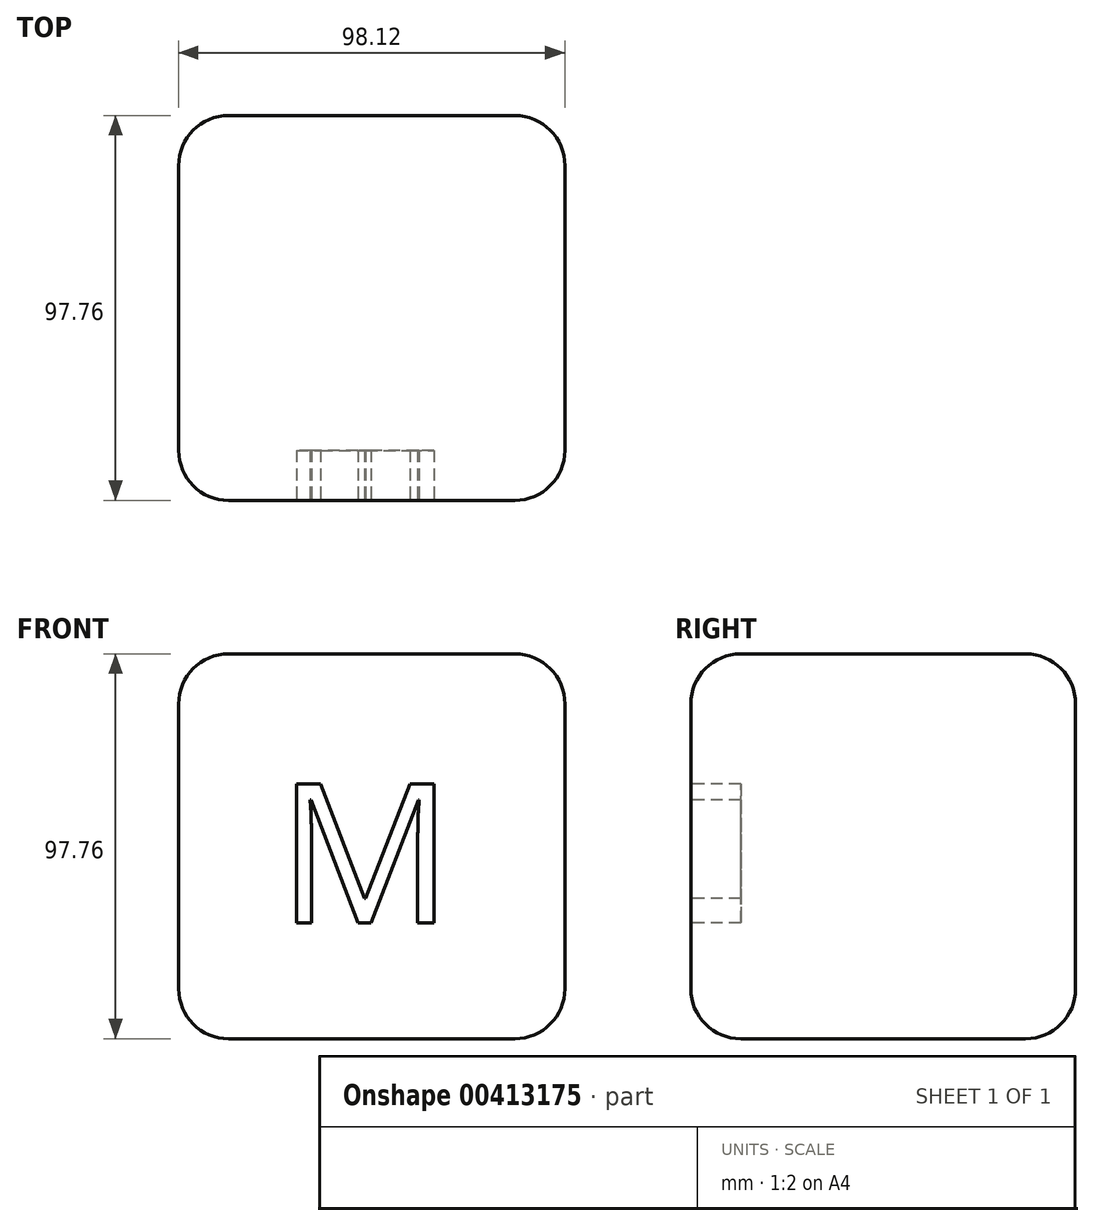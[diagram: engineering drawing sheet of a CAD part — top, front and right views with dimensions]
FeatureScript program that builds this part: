
annotation { "Feature Type Name" : "Feature", "Feature Type Description" : "" }
export const myFeature = defineFeature(function(context is Context, id is Id, definition is map)
    precondition{}
    {
        {
            var Q0;
            Q0=qCreatedBy(makeId("Top.planeOp"),FACE);
            var sketch = newSketch(context, id + "F0", { "sketchPlane" : qUnion([Q0])});
            skLineSegment(sketch, "E0.bottom", {"start": v(-49.06, 48.88) * mm, "end": v(49.06, 48.88) * mm});
            skLineSegment(sketch, "E0.top", {"start": v(-49.06, -48.88) * mm, "end": v(49.06, -48.88) * mm});
            skLineSegment(sketch, "E0.left", {"start": v(-49.06, 48.88) * mm, "end": v(-49.06, -48.88) * mm});
            skLineSegment(sketch, "E0.right", {"start": v(49.06, 48.88) * mm, "end": v(49.06, -48.88) * mm});
            skPoint(sketch, "E0.middle", {"position": v(0, 0) * mm});
            skSolve(sketch);
        }
        {
            var Q0;
            Q0=makeQuery(id+"F0.imprint","IMPRINT",FACE,{"disambiguationData":[TD([[makeQuery(id+"F0.imprint","IMPRINT",EDGE,{"derivedFrom":sQuery(id+"F0.wireOp",EDGE,"E0.bottom")}),-1.0]])]});
            extrude(context, id + "F1", {"entities" : qUnion([Q0]), "depth" : 97.76 * mm});
        }
        {
            var Q0;
            Q0=makeQuery(id+"F1.opExtrude","CAP_EDGE",EDGE,{"disambiguationData":[OSD([sQuery(id+"F0.wireOp",EDGE,"E0.bottom")])],"isStart":false});
            fillet(context, id + "F2", {"entities" : qUnion([Q0]), "radius" : 12.7 * mm, "tangentPropagation" : true, "allowEdgeOverflow" : false});
        }
        {
            var Q0;
            Q0=makeQuery(id+"F1.opExtrude","CAP_EDGE",EDGE,{"disambiguationData":[OSD([sQuery(id+"F0.wireOp",EDGE,"E0.right")])],"isStart":false});
            var Q1;
            Q1=makeQuery(id+"F1.opExtrude","SWEPT_EDGE",EDGE,{"disambiguationData":[OSD([sQuery(id+"F0.wireOp",EDGE,"E0.top"),sQuery(id+"F0.wireOp",EDGE,"E0.right")])]});
            var Q2;
            Q2=makeQuery(id+"F1.opExtrude","CAP_EDGE",EDGE,{"disambiguationData":[OSD([sQuery(id+"F0.wireOp",EDGE,"E0.right")])],"isStart":true});
            var Q3;
            Q3=makeQuery(id+"F1.opExtrude","SWEPT_EDGE",EDGE,{"disambiguationData":[OSD([sQuery(id+"F0.wireOp",EDGE,"E0.bottom"),sQuery(id+"F0.wireOp",EDGE,"E0.right")])]});
            var Q4;
            Q4=makeQuery(id+"F1.opExtrude","CAP_EDGE",EDGE,{"disambiguationData":[OSD([sQuery(id+"F0.wireOp",EDGE,"E0.top")])],"isStart":false});
            var Q5;
            Q5=makeQuery(id+"F1.opExtrude","CAP_EDGE",EDGE,{"disambiguationData":[OSD([sQuery(id+"F0.wireOp",EDGE,"E0.top")])],"isStart":true});
            var Q6;
            Q6=makeQuery(id+"F1.opExtrude","CAP_EDGE",EDGE,{"disambiguationData":[OSD([sQuery(id+"F0.wireOp",EDGE,"E0.bottom")])],"isStart":true});
            var Q7;
            Q7=makeQuery(id+"F1.opExtrude","CAP_EDGE",EDGE,{"disambiguationData":[OSD([sQuery(id+"F0.wireOp",EDGE,"E0.left")])],"isStart":true});
            var Q8;
            Q8=makeQuery(id+"F1.opExtrude","SWEPT_EDGE",EDGE,{"disambiguationData":[OSD([sQuery(id+"F0.wireOp",EDGE,"E0.bottom"),sQuery(id+"F0.wireOp",EDGE,"E0.left")])]});
            var Q9;
            Q9=makeQuery(id+"F1.opExtrude","SWEPT_EDGE",EDGE,{"disambiguationData":[OSD([sQuery(id+"F0.wireOp",EDGE,"E0.top"),sQuery(id+"F0.wireOp",EDGE,"E0.left")])]});
            var Q10;
            Q10=makeQuery(id+"F1.opExtrude","CAP_EDGE",EDGE,{"disambiguationData":[OSD([sQuery(id+"F0.wireOp",EDGE,"E0.left")])],"isStart":false});
            fillet(context, id + "F3", {"entities" : qUnion([Q0, Q1, Q2, Q3, Q4, Q5, Q6, Q7, Q8, Q9, Q10]), "radius" : 12.7 * mm, "tangentPropagation" : true, "allowEdgeOverflow" : false});
        }
        {
            var Q0;
            Q0=makeQuery(id+"F1.opExtrude","SWEPT_FACE",FACE,{"disambiguationData":[OSD([sQuery(id+"F0.wireOp",EDGE,"E0.top")])]});
            var sketch = newSketch(context, id + "F4", { "sketchPlane" : qUnion([Q0])});
            skText(sketch, "E1", { "text": "M", "fontName": "OpenSans-Regular.ttf"});
            const initialGuessF4  = {"E1": [-0.03636, 0.0127, 1, 0, 0.07236]};
            skSetInitialGuess(sketch, initialGuessF4);
            skSolve(sketch);
        }
        {
            var Q0;
            Q0 = qSketchRegion(id + "F4", true);
            var Q1;
            {var subQ0=sQuery(id+"F4.wireOp",EDGE,"E1.sketch_text.stroke-5");Q1=makeQuery(id+"F4.imprint","IMPRINT",FACE,{"disambiguationData":[TD([[makeQuery(id+"F4.imprint","IMPRINT",EDGE,{"derivedFrom":subQ0}),1.0]])]});}
            extrude(context, id + "F5", {"entities" : qUnion([Q0, Q1]), "operationType" : NewBodyOperationType.REMOVE, "depth" : 6.35 * mm});
        }
        {
            var Q0;
            Q0=makeQuery(id+"F1.opExtrude","SWEPT_FACE",FACE,{"disambiguationData":[OSD([sQuery(id+"F0.wireOp",EDGE,"E0.top")])]});
            var sketch = newSketch(context, id + "F6", { "sketchPlane" : qUnion([Q0])});
            skText(sketch, "E2", { "text": "M", "fontName": "OpenSans-Regular.ttf"});
            const initialGuessF6  = {"E2": [-0.02396, 0.02947, 1, 0, 0.03555]};
            skSetInitialGuess(sketch, initialGuessF6);
            skSolve(sketch);
        }
        {
            var Q0;
            Q0 = qSketchRegion(id + "F6", true);
            extrude(context, id + "F7", {"entities" : qUnion([Q0]), "operationType" : NewBodyOperationType.REMOVE, "oppositeDirection" : true, "depth" : 12.7 * mm});
        }
    });
